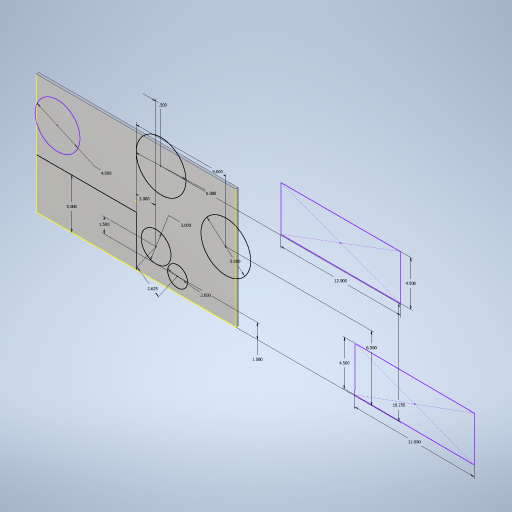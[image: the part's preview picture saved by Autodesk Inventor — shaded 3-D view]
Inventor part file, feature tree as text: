
AUTODESK INVENTOR PART (.ipt)
format: ipt  version: 2023.4 (Build 274418000, 418)  size: 271,872 bytes
history: native  units: in
note: dims shown in document units (in); Inventor stores cm internally (conversion verified against a paired STEP export)
features: sketch x2, extrude x1
ambient origin geometry x8: Origin, YZ Plane, XZ Plane, XY Plane, X Axis, Y Axis, Z Axis, Center Point
bodies: Solid1 (feature_tree)
feature tree (3):
  extrude  "Extrusion1"  Depth=12.0in
  sketch  "Sketch2"  dims[d2=0.25in d3=0.0in d4=5.0in d6=2.0in d7=5.0in d9=12.0in d10=4.5in d11=1.5in d12=6.5in d14=12.0in d15=4.5in d16=4.5in d17=3.0in d18=1.5in d19=2.625in d20=5.0in d21=10.25in d22=2.0in d23=9.0in d24=0.5in]
  sketch  "Sketch1"  dims[d0=20.0in d1=12.0in]
